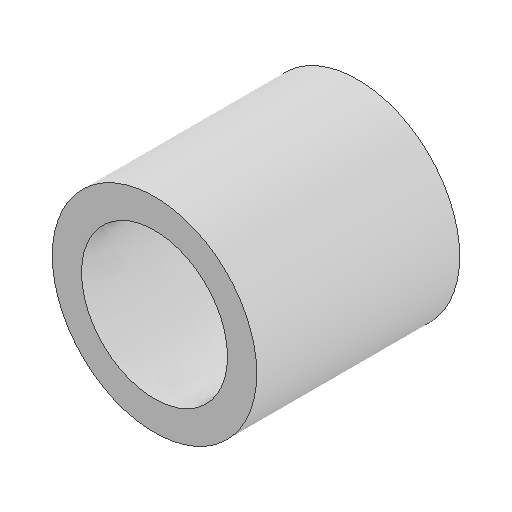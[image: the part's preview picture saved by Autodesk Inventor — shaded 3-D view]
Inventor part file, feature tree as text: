
AUTODESK INVENTOR PART (.ipt)
format: ipt  version: 2025.1 (Build 291241000, 241)  size: 100,352 bytes
history: native  units: mm
features: other x1, extrude x1, sketch x1
ambient origin geometry x8: Origin, YZ Plane, XZ Plane, XY Plane, X Axis, Y Axis, Z Axis, Center Point
bodies: Body1 (feature_tree)
feature tree (3):
  other  "Bryła1"
  extrude  "Wyciągnięcie proste1"  Depth=5.0mm
  sketch  "Szkic1"
